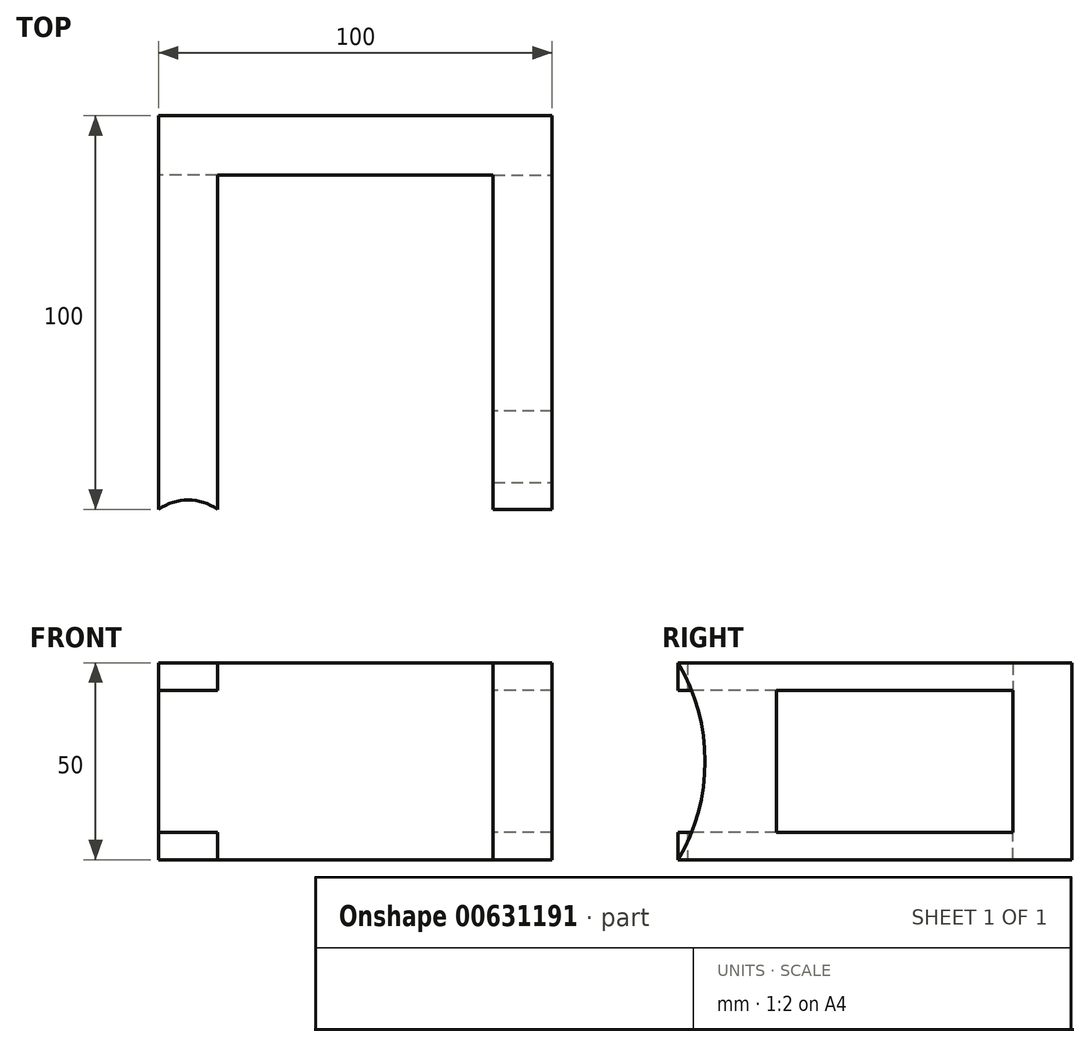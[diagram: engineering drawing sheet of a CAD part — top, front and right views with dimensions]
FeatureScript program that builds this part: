
annotation { "Feature Type Name" : "Feature", "Feature Type Description" : "" }
export const myFeature = defineFeature(function(context is Context, id is Id, definition is map)
    precondition{}
    {
        {
            var Q0;
            Q0=qCreatedBy(makeId("Front.planeOp"),FACE);
            var sketch = newSketch(context, id + "F0", { "sketchPlane" : qUnion([Q0])});
            skLineSegment(sketch, "E0.bottom", {"start": v(0, 0) * mm, "end": v(100, 0) * mm});
            skLineSegment(sketch, "E0.top", {"start": v(0, -50) * mm, "end": v(100, -50) * mm});
            skLineSegment(sketch, "E0.left", {"start": v(0, 0) * mm, "end": v(0, -50) * mm});
            skLineSegment(sketch, "E0.right", {"start": v(100, 0) * mm, "end": v(100, -50) * mm});
            skSolve(sketch);
        }
        {
            var Q0;
            Q0 = qSketchRegion(id + "F0", true);
            extrude(context, id + "F1", {"entities" : qUnion([Q0]), "depth" : 100 * mm, "offsetDistance" : 25 * mm});
        }
        {
            var Q0;
            Q0=makeQuery(id+"F1.opExtrude","CAP_FACE",FACE,{"disambiguationData":[OSD([sQuery(id+"F0.wireOp",EDGE,"E0.bottom"),sQuery(id+"F0.wireOp",EDGE,"E0.top"),sQuery(id+"F0.wireOp",EDGE,"E0.left"),sQuery(id+"F0.wireOp",EDGE,"E0.right")])],"isStart":false});
            var sketch = newSketch(context, id + "F2", { "sketchPlane" : qUnion([Q0])});
            skLineSegment(sketch, "E1", {"start": v(0, 0) * mm, "end": v(15, 0) * mm});
            skLineSegment(sketch, "E2", {"start": v(15, 0) * mm, "end": v(15, -7) * mm});
            skLineSegment(sketch, "E3", {"start": v(15, -7) * mm, "end": v(0, -7) * mm});
            skLineSegment(sketch, "E4.MirrorCS", {"start": v(100, 0) * mm, "end": v(85, 0) * mm});
            skLineSegment(sketch, "E5.MirrorCS", {"start": v(85, 0) * mm, "end": v(85, -7) * mm});
            skLineSegment(sketch, "E6.MirrorCS", {"start": v(85, -7) * mm, "end": v(100, -7) * mm});
            skLineSegment(sketch, "E7.MirrorCS", {"start": v(100, -50) * mm, "end": v(85, -50) * mm});
            skLineSegment(sketch, "E8.MirrorCS", {"start": v(85, -50) * mm, "end": v(85, -43) * mm});
            skLineSegment(sketch, "E9.MirrorCS", {"start": v(15, -43) * mm, "end": v(0, -43) * mm});
            skLineSegment(sketch, "E10.MirrorCS", {"start": v(85, -43) * mm, "end": v(100, -43) * mm});
            skLineSegment(sketch, "E11.MirrorCS", {"start": v(0, -50) * mm, "end": v(15, -50) * mm});
            skLineSegment(sketch, "E12.MirrorCS", {"start": v(15, -50) * mm, "end": v(15, -43) * mm});
            skSolve(sketch);
        }
        {
            var Q0;
            Q0 = qSketchRegion(id + "F2", true);
            var Q1;
            {var subQ4=sQuery(id+"F2.wireOp",EDGE,"E2");Q1=makeQuery(id+"F2.imprint","IMPRINT",FACE,{"disambiguationData":[TD([[makeQuery(id+"F2.imprint","IMPRINT",EDGE,{"derivedFrom":subQ4}),1.0]])]});}
            extrude(context, id + "F3", {"entities" : qUnion([Q0, Q1]), "operationType" : NewBodyOperationType.REMOVE, "oppositeDirection" : true, "depth" : 85 * mm, "offsetDistance" : 25 * mm});
        }
        {
            var Q0;
            {var subQ0=sQuery(id+"F0.wireOp",EDGE,"E0.bottom");var subQ1=sQuery(id+"F0.wireOp",EDGE,"E0.right");Q0=makeQuery(id+"F3.boolean.opBoolean","SPLIT",FACE,{"disambiguationData":[TD([makeQuery(id+"F3.opExtrude","SWEPT_FACE",FACE,{"disambiguationData":[OSD([sQuery(id+"F2.wireOp",EDGE,"E5.MirrorCS")])]})])],"derivedFrom":makeQuery(id+"F1.opExtrude","CAP_FACE",FACE,{"disambiguationData":[OSD([subQ0,sQuery(id+"F0.wireOp",EDGE,"E0.top"),sQuery(id+"F0.wireOp",EDGE,"E0.left"),subQ1])],"isStart":false})});}
            var sketch = newSketch(context, id + "F4", { "sketchPlane" : qUnion([Q0])});
            skLineSegment(sketch, "E13", {"start": v(85, 0) * mm, "end": v(85, -50) * mm});
            skLineSegment(sketch, "E14", {"start": v(85, -50) * mm, "end": v(100, -50) * mm});
            skPoint(sketch, "E14.endSnap0", {"position": v(100, -3.5) * mm});
            skLineSegment(sketch, "E15", {"start": v(100, -50) * mm, "end": v(100, 0) * mm});
            skLineSegment(sketch, "E16", {"start": v(100, 0) * mm, "end": v(85, 0) * mm});
            skSolve(sketch);
        }
        {
            var Q0;
            Q0 = qSketchRegion(id + "F4", true);
            extrude(context, id + "F5", {"entities" : qUnion([Q0]), "operationType" : NewBodyOperationType.ADD, "oppositeDirection" : true, "depth" : 25 * mm, "offsetDistance" : 25 * mm});
        }
        {
            var Q0;
            Q0=makeQuery(id+"F5.boolean.opBoolean","MERGE",FACE,{"derivedFrom":[makeQuery(id+"F1.opExtrude","SWEPT_FACE",FACE,{"disambiguationData":[OSD([sQuery(id+"F0.wireOp",EDGE,"E0.right")])]}),makeQuery(id+"F5.opExtrude","SWEPT_FACE",FACE,{"disambiguationData":[OSD([sQuery(id+"F4.wireOp",EDGE,"E15")])]})]});
            var sketch = newSketch(context, id + "F6", { "sketchPlane" : qUnion([Q0])});
            skArc(sketch, "E17", {"start": v(-100, -50) * mm, "mid": v(-93.16, -25) * mm, "end": v(-100, 0) * mm});
            skLineSegment(sketch, "E18", {"start": v(-100, 0) * mm, "end": v(-100, -50) * mm});
            skSolve(sketch);
        }
        {
            var Q0;
            Q0 = qSketchRegion(id + "F6", true);
            extrude(context, id + "F7", {"entities" : qUnion([Q0]), "operationType" : NewBodyOperationType.REMOVE, "oppositeDirection" : true, "depth" : 15 * mm, "offsetDistance" : 25 * mm});
        }
        {
            var Q0;
            Q0=makeQuery(id+"F1.opExtrude","SWEPT_FACE",FACE,{"disambiguationData":[OSD([sQuery(id+"F0.wireOp",EDGE,"E0.top")])]});
            var sketch = newSketch(context, id + "F8", { "sketchPlane" : qUnion([Q0])});
            skArc(sketch, "E19", {"start": v(0, 100) * mm, "mid": v(7.5, 97.64) * mm, "end": v(15, 100) * mm});
            skLineSegment(sketch, "E20", {"start": v(0, 100) * mm, "end": v(15, 100) * mm});
            skSolve(sketch);
        }
        {
            var Q0;
            Q0 = qSketchRegion(id + "F8", true);
            extrude(context, id + "F9", {"entities" : qUnion([Q0]), "operationType" : NewBodyOperationType.REMOVE, "oppositeDirection" : true, "depth" : 50 * mm, "offsetDistance" : 25 * mm});
        }
    });
